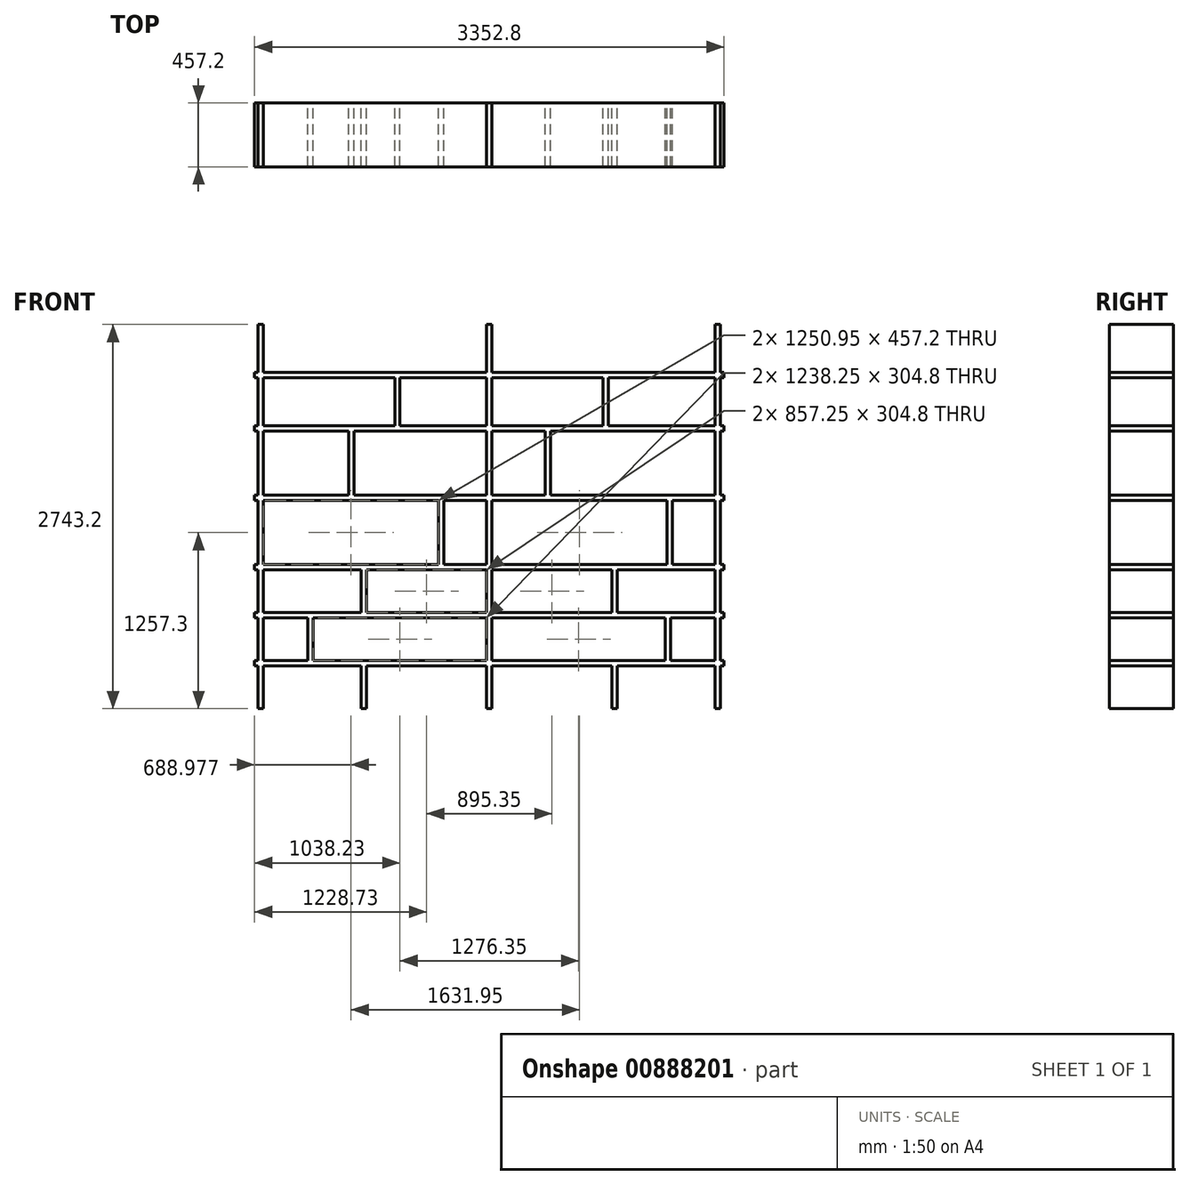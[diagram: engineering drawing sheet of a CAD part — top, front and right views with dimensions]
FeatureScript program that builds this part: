
annotation { "Feature Type Name" : "Feature", "Feature Type Description" : "" }
export const myFeature = defineFeature(function(context is Context, id is Id, definition is map)
    precondition{}
    {
        {
            var Q0;
            Q0=qCreatedBy(makeId("Front.planeOp"),FACE);
            var sketch = newSketch(context, id + "F0", { "sketchPlane" : qUnion([Q0])});
            skLineSegment(sketch, "E0.bottom", {"start": v(-54.9, 2702.76) * mm, "end": v(3297.9, 2702.76) * mm});
            skLineSegment(sketch, "E0.top", {"start": v(-54.9, -40.44) * mm, "end": v(3297.9, -40.44) * mm});
            skLineSegment(sketch, "E0.left", {"start": v(-54.9, 2702.76) * mm, "end": v(-54.9, -40.44) * mm});
            skLineSegment(sketch, "E0.right", {"start": v(3297.9, 2702.76) * mm, "end": v(3297.9, -40.44) * mm});
            skLineSegment(sketch, "E1", {"start": v(-54.9, 264.36) * mm, "end": v(3297.9, 264.36) * mm});
            skLineSegment(sketch, "E2", {"start": v(-54.9, 607.26) * mm, "end": v(3297.9, 607.26) * mm});
            skLineSegment(sketch, "E3", {"start": v(-54.9, 950.16) * mm, "end": v(3297.9, 950.16) * mm});
            skLineSegment(sketch, "E4", {"start": v(-54.9, 645.36) * mm, "end": v(3297.9, 645.36) * mm});
            skLineSegment(sketch, "E5", {"start": v(-54.9, 302.46) * mm, "end": v(3297.9, 302.46) * mm});
            skLineSegment(sketch, "E6", {"start": v(-54.9, 988.26) * mm, "end": v(3297.9, 988.26) * mm});
            skLineSegment(sketch, "E7", {"start": v(-54.9, 1445.46) * mm, "end": v(3297.9, 1445.46) * mm});
            skLineSegment(sketch, "E8", {"start": v(-54.9, 1483.56) * mm, "end": v(3297.9, 1483.56) * mm});
            skLineSegment(sketch, "E9", {"start": v(-54.9, 1940.76) * mm, "end": v(3297.9, 1940.76) * mm});
            skLineSegment(sketch, "E10", {"start": v(-54.9, 1978.86) * mm, "end": v(3297.9, 1978.86) * mm});
            skLineSegment(sketch, "E11", {"start": v(-54.9, 2321.76) * mm, "end": v(3297.9, 2321.76) * mm});
            skLineSegment(sketch, "E12", {"start": v(-54.9, 2359.86) * mm, "end": v(3297.9, 2359.86) * mm});
            skLineSegment(sketch, "E13.bottom", {"start": v(707.1, -40.44) * mm, "end": v(745.2, -40.44) * mm});
            skLineSegment(sketch, "E13.top", {"start": v(707.1, 264.36) * mm, "end": v(745.2, 264.36) * mm});
            skLineSegment(sketch, "E13.left", {"start": v(707.1, -40.44) * mm, "end": v(707.1, 264.36) * mm});
            skLineSegment(sketch, "E13.right", {"start": v(745.2, -40.44) * mm, "end": v(745.2, 264.36) * mm});
            skLineSegment(sketch, "E14.bottom", {"start": v(1602.45, -40.44) * mm, "end": v(1640.55, -40.44) * mm});
            skLineSegment(sketch, "E14.top", {"start": v(1602.45, 264.36) * mm, "end": v(1640.55, 264.36) * mm});
            skLineSegment(sketch, "E14.left", {"start": v(1602.45, -40.44) * mm, "end": v(1602.45, 264.36) * mm});
            skLineSegment(sketch, "E14.right", {"start": v(1640.55, -40.44) * mm, "end": v(1640.55, 264.36) * mm});
            skLineSegment(sketch, "E15.bottom", {"start": v(2497.8, -40.44) * mm, "end": v(2535.9, -40.44) * mm});
            skLineSegment(sketch, "E15.top", {"start": v(2497.8, 264.36) * mm, "end": v(2535.9, 264.36) * mm});
            skLineSegment(sketch, "E15.left", {"start": v(2497.8, -40.44) * mm, "end": v(2497.8, 264.36) * mm});
            skLineSegment(sketch, "E15.right", {"start": v(2535.9, -40.44) * mm, "end": v(2535.9, 264.36) * mm});
            skLineSegment(sketch, "E16.bottom", {"start": v(326.1, 302.46) * mm, "end": v(364.2, 302.46) * mm});
            skLineSegment(sketch, "E16.top", {"start": v(326.1, 607.26) * mm, "end": v(364.2, 607.26) * mm});
            skLineSegment(sketch, "E16.left", {"start": v(326.1, 302.46) * mm, "end": v(326.1, 607.26) * mm});
            skLineSegment(sketch, "E16.right", {"start": v(364.2, 302.46) * mm, "end": v(364.2, 607.26) * mm});
            skLineSegment(sketch, "E17.bottom", {"start": v(1640.55, 607.26) * mm, "end": v(1602.45, 607.26) * mm});
            skLineSegment(sketch, "E17.top", {"start": v(1640.55, 302.46) * mm, "end": v(1602.45, 302.46) * mm});
            skLineSegment(sketch, "E17.left", {"start": v(1640.55, 607.26) * mm, "end": v(1640.55, 302.46) * mm});
            skLineSegment(sketch, "E17.right", {"start": v(1602.45, 607.26) * mm, "end": v(1602.45, 302.46) * mm});
            skLineSegment(sketch, "E18.bottom", {"start": v(2878.8, 607.26) * mm, "end": v(2916.9, 607.26) * mm});
            skLineSegment(sketch, "E18.top", {"start": v(2878.8, 302.46) * mm, "end": v(2916.9, 302.46) * mm});
            skLineSegment(sketch, "E18.left", {"start": v(2878.8, 607.26) * mm, "end": v(2878.8, 302.46) * mm});
            skLineSegment(sketch, "E18.right", {"start": v(2916.9, 607.26) * mm, "end": v(2916.9, 302.46) * mm});
            skLineSegment(sketch, "E19.bottom", {"start": v(1259.55, 988.26) * mm, "end": v(1297.65, 988.26) * mm});
            skLineSegment(sketch, "E19.top", {"start": v(1259.55, 1445.46) * mm, "end": v(1297.65, 1445.46) * mm});
            skLineSegment(sketch, "E19.left", {"start": v(1297.65, 988.26) * mm, "end": v(1297.65, 1445.46) * mm});
            skLineSegment(sketch, "E19.right", {"start": v(1259.55, 1445.46) * mm, "end": v(1259.55, 988.26) * mm});
            skLineSegment(sketch, "E20.bottom", {"start": v(745.2, 950.16) * mm, "end": v(707.1, 950.16) * mm});
            skLineSegment(sketch, "E20.top", {"start": v(745.2, 645.36) * mm, "end": v(707.1, 645.36) * mm});
            skLineSegment(sketch, "E20.left", {"start": v(745.2, 950.16) * mm, "end": v(745.2, 645.36) * mm});
            skLineSegment(sketch, "E20.right", {"start": v(707.1, 950.16) * mm, "end": v(707.1, 645.36) * mm});
            skLineSegment(sketch, "E21.bottom", {"start": v(2497.8, 950.16) * mm, "end": v(2535.9, 950.16) * mm});
            skLineSegment(sketch, "E21.top", {"start": v(2497.8, 645.36) * mm, "end": v(2535.9, 645.36) * mm});
            skLineSegment(sketch, "E21.left", {"start": v(2497.8, 950.16) * mm, "end": v(2497.8, 645.36) * mm});
            skLineSegment(sketch, "E21.right", {"start": v(2535.9, 950.16) * mm, "end": v(2535.9, 645.36) * mm});
            skLineSegment(sketch, "E22.bottom", {"start": v(1602.45, 645.36) * mm, "end": v(1640.55, 645.36) * mm});
            skLineSegment(sketch, "E22.top", {"start": v(1602.45, 950.16) * mm, "end": v(1640.55, 950.16) * mm});
            skLineSegment(sketch, "E22.left", {"start": v(1602.45, 645.36) * mm, "end": v(1602.45, 950.16) * mm});
            skLineSegment(sketch, "E22.right", {"start": v(1640.55, 645.36) * mm, "end": v(1640.55, 950.16) * mm});
            skLineSegment(sketch, "E23.bottom", {"start": v(3272.5, 2702.76) * mm, "end": v(3234.4, 2702.76) * mm});
            skLineSegment(sketch, "E23.top", {"start": v(3272.5, -40.44) * mm, "end": v(3234.4, -40.44) * mm});
            skLineSegment(sketch, "E23.left", {"start": v(3272.5, 2702.76) * mm, "end": v(3272.5, -40.44) * mm});
            skLineSegment(sketch, "E23.right", {"start": v(3234.4, 2702.76) * mm, "end": v(3234.4, -40.44) * mm});
            skLineSegment(sketch, "E24.bottom", {"start": v(8.6, 2702.76) * mm, "end": v(-29.5, 2702.76) * mm});
            skLineSegment(sketch, "E24.top", {"start": v(8.6, -40.44) * mm, "end": v(-29.5, -40.44) * mm});
            skLineSegment(sketch, "E24.left", {"start": v(8.6, 2702.76) * mm, "end": v(8.6, -40.44) * mm});
            skLineSegment(sketch, "E24.right", {"start": v(-29.5, 2702.76) * mm, "end": v(-29.5, -40.44) * mm});
            skLineSegment(sketch, "E25.bottom", {"start": v(1640.55, 950.16) * mm, "end": v(1602.45, 950.16) * mm});
            skLineSegment(sketch, "E25.top", {"start": v(1640.55, 2702.76) * mm, "end": v(1602.45, 2702.76) * mm});
            skLineSegment(sketch, "E25.left", {"start": v(1640.55, 950.16) * mm, "end": v(1640.55, 2702.76) * mm});
            skLineSegment(sketch, "E25.right", {"start": v(1602.45, 950.16) * mm, "end": v(1602.45, 2702.76) * mm});
            skLineSegment(sketch, "E26.bottom", {"start": v(2891.5, 1445.46) * mm, "end": v(2929.6, 1445.46) * mm});
            skLineSegment(sketch, "E26.top", {"start": v(2891.5, 988.26) * mm, "end": v(2929.6, 988.26) * mm});
            skLineSegment(sketch, "E26.left", {"start": v(2891.5, 1445.46) * mm, "end": v(2891.5, 988.26) * mm});
            skLineSegment(sketch, "E26.right", {"start": v(2929.6, 1445.46) * mm, "end": v(2929.6, 988.26) * mm});
            skLineSegment(sketch, "E27.bottom", {"start": v(2021.55, 1483.56) * mm, "end": v(2059.65, 1483.56) * mm});
            skLineSegment(sketch, "E27.top", {"start": v(2021.55, 1940.76) * mm, "end": v(2059.65, 1940.76) * mm});
            skLineSegment(sketch, "E27.left", {"start": v(2021.55, 1483.56) * mm, "end": v(2021.55, 1940.76) * mm});
            skLineSegment(sketch, "E27.right", {"start": v(2059.65, 1483.56) * mm, "end": v(2059.65, 1940.76) * mm});
            skLineSegment(sketch, "E28.bottom", {"start": v(656.3, 1483.56) * mm, "end": v(618.2, 1483.56) * mm});
            skLineSegment(sketch, "E28.top", {"start": v(656.3, 1940.76) * mm, "end": v(618.2, 1940.76) * mm});
            skLineSegment(sketch, "E28.left", {"start": v(656.3, 1483.56) * mm, "end": v(656.3, 1940.76) * mm});
            skLineSegment(sketch, "E28.right", {"start": v(618.2, 1483.56) * mm, "end": v(618.2, 1940.76) * mm});
            skLineSegment(sketch, "E29.bottom", {"start": v(2472.4, 1978.86) * mm, "end": v(2434.3, 1978.86) * mm});
            skLineSegment(sketch, "E29.top", {"start": v(2472.4, 2321.76) * mm, "end": v(2434.3, 2321.76) * mm});
            skLineSegment(sketch, "E29.left", {"start": v(2472.4, 1978.86) * mm, "end": v(2472.4, 2321.76) * mm});
            skLineSegment(sketch, "E29.right", {"start": v(2434.3, 1978.86) * mm, "end": v(2434.3, 2321.76) * mm});
            skLineSegment(sketch, "E30.bottom", {"start": v(983.52, 2321.76) * mm, "end": v(945.42, 2321.76) * mm});
            skLineSegment(sketch, "E30.top", {"start": v(983.52, 1978.86) * mm, "end": v(945.42, 1978.86) * mm});
            skLineSegment(sketch, "E30.left", {"start": v(983.52, 2321.76) * mm, "end": v(983.52, 1978.86) * mm});
            skLineSegment(sketch, "E30.right", {"start": v(945.42, 2321.76) * mm, "end": v(945.42, 1978.86) * mm});
            skSolve(sketch);
        }
        {
            var Q0;
            {var subQ0=sQuery(id+"F0.wireOp",EDGE,"E24.left");var subQ1=sQuery(id+"F0.wireOp",EDGE,"E0.bottom");var subQ2=makeQuery(id+"F0.imprint","INTERSECT",VERTEX,{"derivedFrom":[subQ1,subQ0]});Q0=makeQuery(id+"F0.imprint","IMPRINT",FACE,{"disambiguationData":[TD([[makeQuery(id+"F0.imprint","IMPRINT",EDGE,{"disambiguationData":[TD([[subQ2,1.0]])],"derivedFrom":subQ1}),-1.0]])]});}
            var Q1;
            {var subQ0=sQuery(id+"F0.wireOp",EDGE,"E11");var subQ1=sQuery(id+"F0.wireOp",EDGE,"E0.left");var subQ2=makeQuery(id+"F0.imprint","INTERSECT",VERTEX,{"derivedFrom":[subQ1,subQ0]});Q1=makeQuery(id+"F0.imprint","IMPRINT",FACE,{"disambiguationData":[TD([[makeQuery(id+"F0.imprint","IMPRINT",EDGE,{"disambiguationData":[TD([[subQ2,1.0]])],"derivedFrom":subQ1}),1.0]])]});}
            var Q2;
            {var subQ0=sQuery(id+"F0.wireOp",EDGE,"E24.left");var subQ1=sQuery(id+"F0.wireOp",EDGE,"E11");var subQ2=makeQuery(id+"F0.imprint","INTERSECT",VERTEX,{"derivedFrom":[subQ1,subQ0]});Q2=makeQuery(id+"F0.imprint","IMPRINT",FACE,{"disambiguationData":[TD([[makeQuery(id+"F0.imprint","IMPRINT",EDGE,{"disambiguationData":[TD([[subQ2,1.0]])],"derivedFrom":subQ1}),1.0]])]});}
            var Q3;
            {var subQ3=sQuery(id+"F0.wireOp",EDGE,"E24.left");var subQ5=sQuery(id+"F0.wireOp",EDGE,"E11");var subQ8=makeQuery(id+"F0.imprint","INTERSECT",VERTEX,{"derivedFrom":[subQ5,subQ3]});Q3=makeQuery(id+"F0.imprint","IMPRINT",FACE,{"disambiguationData":[TD([[makeQuery(id+"F0.imprint","IMPRINT",EDGE,{"disambiguationData":[TD([[subQ8,-1.0]])],"derivedFrom":subQ5}),1.0]])]});}
            var Q4;
            {var subQ0=sQuery(id+"F0.wireOp",EDGE,"E24.left");var subQ1=sQuery(id+"F0.wireOp",EDGE,"E10");var subQ2=makeQuery(id+"F0.imprint","INTERSECT",VERTEX,{"derivedFrom":[subQ1,subQ0]});Q4=makeQuery(id+"F0.imprint","IMPRINT",FACE,{"disambiguationData":[TD([[makeQuery(id+"F0.imprint","IMPRINT",EDGE,{"disambiguationData":[TD([[subQ2,1.0]])],"derivedFrom":subQ1}),1.0]])]});}
            var Q5;
            {var subQ0=sQuery(id+"F0.wireOp",EDGE,"E25.left");var subQ1=sQuery(id+"F0.wireOp",EDGE,"E0.bottom");var subQ2=makeQuery(id+"F0.imprint","INTERSECT",VERTEX,{"derivedFrom":[subQ1,subQ0]});Q5=makeQuery(id+"F0.imprint","IMPRINT",FACE,{"disambiguationData":[TD([[makeQuery(id+"F0.imprint","IMPRINT",EDGE,{"disambiguationData":[TD([[subQ2,1.0]])],"derivedFrom":subQ1}),-1.0]])]});}
            var Q6;
            {var subQ0=sQuery(id+"F0.wireOp",EDGE,"E25.left");var subQ1=sQuery(id+"F0.wireOp",EDGE,"E11");var subQ2=makeQuery(id+"F0.imprint","INTERSECT",VERTEX,{"derivedFrom":[subQ1,subQ0]});Q6=makeQuery(id+"F0.imprint","IMPRINT",FACE,{"disambiguationData":[TD([[makeQuery(id+"F0.imprint","IMPRINT",EDGE,{"disambiguationData":[TD([[subQ2,1.0]])],"derivedFrom":subQ1}),1.0]])]});}
            var Q7;
            {var subQ0=sQuery(id+"F0.wireOp",EDGE,"E11");var subQ8=makeQuery(id+"F0.imprint","INTERSECT",VERTEX,{"derivedFrom":[subQ0,sQuery(id+"F0.wireOp",EDGE,"E29.right")]});Q7=makeQuery(id+"F0.imprint","IMPRINT",FACE,{"disambiguationData":[TD([[makeQuery(id+"F0.imprint","IMPRINT",EDGE,{"disambiguationData":[TD([[subQ8,1.0]])],"derivedFrom":subQ0}),1.0]])]});}
            var Q8;
            {var subQ0=sQuery(id+"F0.wireOp",EDGE,"E25.left");var subQ1=sQuery(id+"F0.wireOp",EDGE,"E10");var subQ2=makeQuery(id+"F0.imprint","INTERSECT",VERTEX,{"derivedFrom":[subQ1,subQ0]});Q8=makeQuery(id+"F0.imprint","IMPRINT",FACE,{"disambiguationData":[TD([[makeQuery(id+"F0.imprint","IMPRINT",EDGE,{"disambiguationData":[TD([[subQ2,1.0]])],"derivedFrom":subQ1}),1.0]])]});}
            var Q9;
            {var subQ0=sQuery(id+"F0.wireOp",EDGE,"E30.left");Q9=makeQuery(id+"F0.imprint","IMPRINT",FACE,{"disambiguationData":[TD([[makeQuery(id+"F0.imprint","IMPRINT",EDGE,{"derivedFrom":subQ0}),-1.0]])]});}
            var Q10;
            {var subQ0=sQuery(id+"F0.wireOp",EDGE,"E9");var subQ1=makeQuery(id+"F0.imprint","INTERSECT",VERTEX,{"derivedFrom":[subQ0,sQuery(id+"F0.wireOp",EDGE,"E28.left")]});Q10=makeQuery(id+"F0.imprint","IMPRINT",FACE,{"disambiguationData":[TD([[makeQuery(id+"F0.imprint","IMPRINT",EDGE,{"disambiguationData":[TD([[subQ1,-1.0]])],"derivedFrom":subQ0}),1.0]])]});}
            var Q11;
            {var subQ0=sQuery(id+"F0.wireOp",EDGE,"E24.left");var subQ1=sQuery(id+"F0.wireOp",EDGE,"E9");var subQ2=makeQuery(id+"F0.imprint","INTERSECT",VERTEX,{"derivedFrom":[subQ1,subQ0]});Q11=makeQuery(id+"F0.imprint","IMPRINT",FACE,{"disambiguationData":[TD([[makeQuery(id+"F0.imprint","IMPRINT",EDGE,{"disambiguationData":[TD([[subQ2,1.0]])],"derivedFrom":subQ1}),1.0]])]});}
            var Q12;
            {var subQ0=sQuery(id+"F0.wireOp",EDGE,"E9");var subQ1=sQuery(id+"F0.wireOp",EDGE,"E0.left");var subQ2=makeQuery(id+"F0.imprint","INTERSECT",VERTEX,{"derivedFrom":[subQ1,subQ0]});Q12=makeQuery(id+"F0.imprint","IMPRINT",FACE,{"disambiguationData":[TD([[makeQuery(id+"F0.imprint","IMPRINT",EDGE,{"disambiguationData":[TD([[subQ2,1.0]])],"derivedFrom":subQ1}),1.0]])]});}
            var Q13;
            {var subQ0=sQuery(id+"F0.wireOp",EDGE,"E24.left");var subQ1=sQuery(id+"F0.wireOp",EDGE,"E8");var subQ2=makeQuery(id+"F0.imprint","INTERSECT",VERTEX,{"derivedFrom":[subQ1,subQ0]});Q13=makeQuery(id+"F0.imprint","IMPRINT",FACE,{"disambiguationData":[TD([[makeQuery(id+"F0.imprint","IMPRINT",EDGE,{"disambiguationData":[TD([[subQ2,1.0]])],"derivedFrom":subQ1}),1.0]])]});}
            var Q14;
            {var subQ0=sQuery(id+"F0.wireOp",EDGE,"E28.left");Q14=makeQuery(id+"F0.imprint","IMPRINT",FACE,{"disambiguationData":[TD([[makeQuery(id+"F0.imprint","IMPRINT",EDGE,{"derivedFrom":subQ0}),1.0]])]});}
            var Q15;
            {var subQ0=sQuery(id+"F0.wireOp",EDGE,"E24.left");var subQ1=sQuery(id+"F0.wireOp",EDGE,"E7");var subQ2=makeQuery(id+"F0.imprint","INTERSECT",VERTEX,{"derivedFrom":[subQ1,subQ0]});Q15=makeQuery(id+"F0.imprint","IMPRINT",FACE,{"disambiguationData":[TD([[makeQuery(id+"F0.imprint","IMPRINT",EDGE,{"disambiguationData":[TD([[subQ2,1.0]])],"derivedFrom":subQ1}),1.0]])]});}
            var Q16;
            {var subQ4=sQuery(id+"F0.wireOp",EDGE,"E7");var subQ5=makeQuery(id+"F0.imprint","INTERSECT",VERTEX,{"derivedFrom":[subQ4,sQuery(id+"F0.wireOp",EDGE,"E19.right")]});Q16=makeQuery(id+"F0.imprint","IMPRINT",FACE,{"disambiguationData":[TD([[makeQuery(id+"F0.imprint","IMPRINT",EDGE,{"disambiguationData":[TD([[subQ5,1.0]])],"derivedFrom":subQ4}),1.0]])]});}
            var Q17;
            {var subQ0=sQuery(id+"F0.wireOp",EDGE,"E24.left");var subQ1=sQuery(id+"F0.wireOp",EDGE,"E6");var subQ2=makeQuery(id+"F0.imprint","INTERSECT",VERTEX,{"derivedFrom":[subQ1,subQ0]});Q17=makeQuery(id+"F0.imprint","IMPRINT",FACE,{"disambiguationData":[TD([[makeQuery(id+"F0.imprint","IMPRINT",EDGE,{"disambiguationData":[TD([[subQ2,1.0]])],"derivedFrom":subQ1}),1.0]])]});}
            var Q18;
            {var subQ0=sQuery(id+"F0.wireOp",EDGE,"E7");var subQ1=sQuery(id+"F0.wireOp",EDGE,"E0.left");var subQ2=makeQuery(id+"F0.imprint","INTERSECT",VERTEX,{"derivedFrom":[subQ1,subQ0]});Q18=makeQuery(id+"F0.imprint","IMPRINT",FACE,{"disambiguationData":[TD([[makeQuery(id+"F0.imprint","IMPRINT",EDGE,{"disambiguationData":[TD([[subQ2,1.0]])],"derivedFrom":subQ1}),1.0]])]});}
            var Q19;
            {var subQ0=sQuery(id+"F0.wireOp",EDGE,"E3");var subQ1=sQuery(id+"F0.wireOp",EDGE,"E0.left");var subQ2=makeQuery(id+"F0.imprint","INTERSECT",VERTEX,{"derivedFrom":[subQ1,subQ0]});Q19=makeQuery(id+"F0.imprint","IMPRINT",FACE,{"disambiguationData":[TD([[makeQuery(id+"F0.imprint","IMPRINT",EDGE,{"disambiguationData":[TD([[subQ2,1.0]])],"derivedFrom":subQ1}),1.0]])]});}
            var Q20;
            {var subQ0=sQuery(id+"F0.wireOp",EDGE,"E2");var subQ1=sQuery(id+"F0.wireOp",EDGE,"E0.left");var subQ2=makeQuery(id+"F0.imprint","INTERSECT",VERTEX,{"derivedFrom":[subQ1,subQ0]});Q20=makeQuery(id+"F0.imprint","IMPRINT",FACE,{"disambiguationData":[TD([[makeQuery(id+"F0.imprint","IMPRINT",EDGE,{"disambiguationData":[TD([[subQ2,1.0]])],"derivedFrom":subQ1}),1.0]])]});}
            var Q21;
            {var subQ0=sQuery(id+"F0.wireOp",EDGE,"E24.left");var subQ1=sQuery(id+"F0.wireOp",EDGE,"E0.top");var subQ2=makeQuery(id+"F0.imprint","INTERSECT",VERTEX,{"derivedFrom":[subQ1,subQ0]});Q21=makeQuery(id+"F0.imprint","IMPRINT",FACE,{"disambiguationData":[TD([[makeQuery(id+"F0.imprint","IMPRINT",EDGE,{"disambiguationData":[TD([[subQ2,1.0]])],"derivedFrom":subQ1}),1.0]])]});}
            var Q22;
            {var subQ0=sQuery(id+"F0.wireOp",EDGE,"E5");var subQ1=sQuery(id+"F0.wireOp",EDGE,"E0.left");var subQ2=makeQuery(id+"F0.imprint","INTERSECT",VERTEX,{"derivedFrom":[subQ1,subQ0]});Q22=makeQuery(id+"F0.imprint","IMPRINT",FACE,{"disambiguationData":[TD([[makeQuery(id+"F0.imprint","IMPRINT",EDGE,{"disambiguationData":[TD([[subQ2,-1.0]])],"derivedFrom":subQ1}),1.0]])]});}
            var Q23;
            {var subQ0=sQuery(id+"F0.wireOp",EDGE,"E24.left");var subQ1=sQuery(id+"F0.wireOp",EDGE,"E1");var subQ2=makeQuery(id+"F0.imprint","INTERSECT",VERTEX,{"derivedFrom":[subQ1,subQ0]});Q23=makeQuery(id+"F0.imprint","IMPRINT",FACE,{"disambiguationData":[TD([[makeQuery(id+"F0.imprint","IMPRINT",EDGE,{"disambiguationData":[TD([[subQ2,1.0]])],"derivedFrom":subQ1}),1.0]])]});}
            var Q24;
            {var subQ0=sQuery(id+"F0.wireOp",EDGE,"E24.left");var subQ1=sQuery(id+"F0.wireOp",EDGE,"E2");var subQ2=makeQuery(id+"F0.imprint","INTERSECT",VERTEX,{"derivedFrom":[subQ1,subQ0]});Q24=makeQuery(id+"F0.imprint","IMPRINT",FACE,{"disambiguationData":[TD([[makeQuery(id+"F0.imprint","IMPRINT",EDGE,{"disambiguationData":[TD([[subQ2,1.0]])],"derivedFrom":subQ1}),-1.0]])]});}
            var Q25;
            {var subQ0=sQuery(id+"F0.wireOp",EDGE,"E24.left");var subQ1=sQuery(id+"F0.wireOp",EDGE,"E2");var subQ2=makeQuery(id+"F0.imprint","INTERSECT",VERTEX,{"derivedFrom":[subQ1,subQ0]});Q25=makeQuery(id+"F0.imprint","IMPRINT",FACE,{"disambiguationData":[TD([[makeQuery(id+"F0.imprint","IMPRINT",EDGE,{"disambiguationData":[TD([[subQ2,1.0]])],"derivedFrom":subQ1}),1.0]])]});}
            var Q26;
            {var subQ0=sQuery(id+"F0.wireOp",EDGE,"E24.left");var subQ1=sQuery(id+"F0.wireOp",EDGE,"E3");var subQ2=makeQuery(id+"F0.imprint","INTERSECT",VERTEX,{"derivedFrom":[subQ1,subQ0]});Q26=makeQuery(id+"F0.imprint","IMPRINT",FACE,{"disambiguationData":[TD([[makeQuery(id+"F0.imprint","IMPRINT",EDGE,{"disambiguationData":[TD([[subQ2,1.0]])],"derivedFrom":subQ1}),-1.0]])]});}
            var Q27;
            {var subQ0=sQuery(id+"F0.wireOp",EDGE,"E2");var subQ1=makeQuery(id+"F0.imprint","INTERSECT",VERTEX,{"derivedFrom":[subQ0,sQuery(id+"F0.wireOp",EDGE,"E16.right")]});Q27=makeQuery(id+"F0.imprint","IMPRINT",FACE,{"disambiguationData":[TD([[makeQuery(id+"F0.imprint","IMPRINT",EDGE,{"disambiguationData":[TD([[subQ1,-1.0]])],"derivedFrom":subQ0}),1.0]])]});}
            var Q28;
            {var subQ4=sQuery(id+"F0.wireOp",EDGE,"E3");var subQ8=makeQuery(id+"F0.imprint","INTERSECT",VERTEX,{"derivedFrom":[subQ4,sQuery(id+"F0.wireOp",EDGE,"E20.right")]});Q28=makeQuery(id+"F0.imprint","IMPRINT",FACE,{"disambiguationData":[TD([[makeQuery(id+"F0.imprint","IMPRINT",EDGE,{"disambiguationData":[TD([[subQ8,1.0]])],"derivedFrom":subQ4}),1.0]])]});}
            var Q29;
            {var subQ0=sQuery(id+"F0.wireOp",EDGE,"E20.left");Q29=makeQuery(id+"F0.imprint","IMPRINT",FACE,{"disambiguationData":[TD([[makeQuery(id+"F0.imprint","IMPRINT",EDGE,{"derivedFrom":subQ0}),-1.0]])]});}
            var Q30;
            {var subQ0=sQuery(id+"F0.wireOp",EDGE,"E24.left");var subQ1=sQuery(id+"F0.wireOp",EDGE,"E3");var subQ2=makeQuery(id+"F0.imprint","INTERSECT",VERTEX,{"derivedFrom":[subQ1,subQ0]});Q30=makeQuery(id+"F0.imprint","IMPRINT",FACE,{"disambiguationData":[TD([[makeQuery(id+"F0.imprint","IMPRINT",EDGE,{"disambiguationData":[TD([[subQ2,1.0]])],"derivedFrom":subQ1}),1.0]])]});}
            var Q31;
            {var subQ2=sQuery(id+"F0.wireOp",EDGE,"E16.left");Q31=makeQuery(id+"F0.imprint","IMPRINT",FACE,{"disambiguationData":[TD([[makeQuery(id+"F0.imprint","IMPRINT",EDGE,{"derivedFrom":subQ2}),-1.0]])]});}
            var Q32;
            {var subQ0=sQuery(id+"F0.wireOp",EDGE,"E1");var subQ7=makeQuery(id+"F0.imprint","INTERSECT",VERTEX,{"derivedFrom":[subQ0,sQuery(id+"F0.wireOp",EDGE,"E14.right")]});Q32=makeQuery(id+"F0.imprint","IMPRINT",FACE,{"disambiguationData":[TD([[makeQuery(id+"F0.imprint","IMPRINT",EDGE,{"disambiguationData":[TD([[subQ7,-1.0]])],"derivedFrom":subQ0}),1.0]])]});}
            var Q33;
            {var subQ0=sQuery(id+"F0.wireOp",EDGE,"E13.left");Q33=makeQuery(id+"F0.imprint","IMPRINT",FACE,{"disambiguationData":[TD([[makeQuery(id+"F0.imprint","IMPRINT",EDGE,{"derivedFrom":subQ0}),-1.0]])]});}
            var Q34;
            {var subQ0=sQuery(id+"F0.wireOp",EDGE,"E19.left");Q34=makeQuery(id+"F0.imprint","IMPRINT",FACE,{"disambiguationData":[TD([[makeQuery(id+"F0.imprint","IMPRINT",EDGE,{"derivedFrom":subQ0}),1.0]])]});}
            var Q35;
            {var subQ0=sQuery(id+"F0.wireOp",EDGE,"E25.right");var subQ1=sQuery(id+"F0.wireOp",EDGE,"E9");var subQ2=makeQuery(id+"F0.imprint","INTERSECT",VERTEX,{"derivedFrom":[subQ1,subQ0]});Q35=makeQuery(id+"F0.imprint","IMPRINT",FACE,{"disambiguationData":[TD([[makeQuery(id+"F0.imprint","IMPRINT",EDGE,{"disambiguationData":[TD([[subQ2,-1.0]])],"derivedFrom":subQ1}),1.0]])]});}
            var Q36;
            {var subQ0=sQuery(id+"F0.wireOp",EDGE,"E25.right");var subQ1=sQuery(id+"F0.wireOp",EDGE,"E8");var subQ2=makeQuery(id+"F0.imprint","INTERSECT",VERTEX,{"derivedFrom":[subQ1,subQ0]});Q36=makeQuery(id+"F0.imprint","IMPRINT",FACE,{"disambiguationData":[TD([[makeQuery(id+"F0.imprint","IMPRINT",EDGE,{"disambiguationData":[TD([[subQ2,-1.0]])],"derivedFrom":subQ1}),1.0]])]});}
            var Q37;
            {var subQ0=sQuery(id+"F0.wireOp",EDGE,"E25.left");var subQ1=sQuery(id+"F0.wireOp",EDGE,"E7");var subQ2=makeQuery(id+"F0.imprint","INTERSECT",VERTEX,{"derivedFrom":[subQ1,subQ0]});Q37=makeQuery(id+"F0.imprint","IMPRINT",FACE,{"disambiguationData":[TD([[makeQuery(id+"F0.imprint","IMPRINT",EDGE,{"disambiguationData":[TD([[subQ2,1.0]])],"derivedFrom":subQ1}),1.0]])]});}
            var Q38;
            {var subQ0=sQuery(id+"F0.wireOp",EDGE,"E25.left");var subQ1=sQuery(id+"F0.wireOp",EDGE,"E6");var subQ2=makeQuery(id+"F0.imprint","INTERSECT",VERTEX,{"derivedFrom":[subQ1,subQ0]});Q38=makeQuery(id+"F0.imprint","IMPRINT",FACE,{"disambiguationData":[TD([[makeQuery(id+"F0.imprint","IMPRINT",EDGE,{"disambiguationData":[TD([[subQ2,1.0]])],"derivedFrom":subQ1}),1.0]])]});}
            var Q39;
            {var subQ0=sQuery(id+"F0.wireOp",EDGE,"E25.left");var subQ5=sQuery(id+"F0.wireOp",EDGE,"E6");var subQ6=makeQuery(id+"F0.imprint","INTERSECT",VERTEX,{"derivedFrom":[subQ5,subQ0]});Q39=makeQuery(id+"F0.imprint","IMPRINT",FACE,{"disambiguationData":[TD([[makeQuery(id+"F0.imprint","IMPRINT",EDGE,{"disambiguationData":[TD([[subQ6,1.0]])],"derivedFrom":subQ5}),-1.0]])]});}
            var Q40;
            {var subQ2=sQuery(id+"F0.wireOp",EDGE,"E22.left");Q40=makeQuery(id+"F0.imprint","IMPRINT",FACE,{"disambiguationData":[TD([[makeQuery(id+"F0.imprint","IMPRINT",EDGE,{"derivedFrom":subQ2}),-1.0]])]});}
            var Q41;
            {var subQ0=sQuery(id+"F0.wireOp",EDGE,"E17.left");Q41=makeQuery(id+"F0.imprint","IMPRINT",FACE,{"disambiguationData":[TD([[makeQuery(id+"F0.imprint","IMPRINT",EDGE,{"derivedFrom":subQ0}),-1.0]])]});}
            var Q42;
            {var subQ2=sQuery(id+"F0.wireOp",EDGE,"E14.left");Q42=makeQuery(id+"F0.imprint","IMPRINT",FACE,{"disambiguationData":[TD([[makeQuery(id+"F0.imprint","IMPRINT",EDGE,{"derivedFrom":subQ2}),-1.0]])]});}
            var Q43;
            {var subQ2=sQuery(id+"F0.wireOp",EDGE,"E27.left");Q43=makeQuery(id+"F0.imprint","IMPRINT",FACE,{"disambiguationData":[TD([[makeQuery(id+"F0.imprint","IMPRINT",EDGE,{"derivedFrom":subQ2}),-1.0]])]});}
            var Q44;
            {var subQ4=sQuery(id+"F0.wireOp",EDGE,"E9");var subQ5=makeQuery(id+"F0.imprint","INTERSECT",VERTEX,{"derivedFrom":[subQ4,sQuery(id+"F0.wireOp",EDGE,"E27.right")]});Q44=makeQuery(id+"F0.imprint","IMPRINT",FACE,{"disambiguationData":[TD([[makeQuery(id+"F0.imprint","IMPRINT",EDGE,{"disambiguationData":[TD([[subQ5,-1.0]])],"derivedFrom":subQ4}),1.0]])]});}
            var Q45;
            {var subQ0=sQuery(id+"F0.wireOp",EDGE,"E29.left");Q45=makeQuery(id+"F0.imprint","IMPRINT",FACE,{"disambiguationData":[TD([[makeQuery(id+"F0.imprint","IMPRINT",EDGE,{"derivedFrom":subQ0}),1.0]])]});}
            var Q46;
            {var subQ0=sQuery(id+"F0.wireOp",EDGE,"E23.right");var subQ1=sQuery(id+"F0.wireOp",EDGE,"E0.bottom");var subQ2=makeQuery(id+"F0.imprint","INTERSECT",VERTEX,{"derivedFrom":[subQ1,subQ0]});Q46=makeQuery(id+"F0.imprint","IMPRINT",FACE,{"disambiguationData":[TD([[makeQuery(id+"F0.imprint","IMPRINT",EDGE,{"disambiguationData":[TD([[subQ2,-1.0]])],"derivedFrom":subQ1}),-1.0]])]});}
            var Q47;
            {var subQ0=sQuery(id+"F0.wireOp",EDGE,"E23.right");var subQ1=sQuery(id+"F0.wireOp",EDGE,"E10");var subQ2=makeQuery(id+"F0.imprint","INTERSECT",VERTEX,{"derivedFrom":[subQ1,subQ0]});Q47=makeQuery(id+"F0.imprint","IMPRINT",FACE,{"disambiguationData":[TD([[makeQuery(id+"F0.imprint","IMPRINT",EDGE,{"disambiguationData":[TD([[subQ2,-1.0]])],"derivedFrom":subQ1}),1.0]])]});}
            var Q48;
            {var subQ0=sQuery(id+"F0.wireOp",EDGE,"E23.right");var subQ1=sQuery(id+"F0.wireOp",EDGE,"E8");var subQ2=makeQuery(id+"F0.imprint","INTERSECT",VERTEX,{"derivedFrom":[subQ1,subQ0]});Q48=makeQuery(id+"F0.imprint","IMPRINT",FACE,{"disambiguationData":[TD([[makeQuery(id+"F0.imprint","IMPRINT",EDGE,{"disambiguationData":[TD([[subQ2,-1.0]])],"derivedFrom":subQ1}),1.0]])]});}
            var Q49;
            {var subQ0=sQuery(id+"F0.wireOp",EDGE,"E26.left");Q49=makeQuery(id+"F0.imprint","IMPRINT",FACE,{"disambiguationData":[TD([[makeQuery(id+"F0.imprint","IMPRINT",EDGE,{"derivedFrom":subQ0}),1.0]])]});}
            var Q50;
            {var subQ4=sQuery(id+"F0.wireOp",EDGE,"E25.left");var subQ5=sQuery(id+"F0.wireOp",EDGE,"E7");var subQ6=makeQuery(id+"F0.imprint","INTERSECT",VERTEX,{"derivedFrom":[subQ5,subQ4]});Q50=makeQuery(id+"F0.imprint","IMPRINT",FACE,{"disambiguationData":[TD([[makeQuery(id+"F0.imprint","IMPRINT",EDGE,{"disambiguationData":[TD([[subQ6,-1.0]])],"derivedFrom":subQ5}),1.0]])]});}
            var Q51;
            {var subQ4=sQuery(id+"F0.wireOp",EDGE,"E3");var subQ7=makeQuery(id+"F0.imprint","INTERSECT",VERTEX,{"derivedFrom":[subQ4,sQuery(id+"F0.wireOp",EDGE,"E21.right")]});Q51=makeQuery(id+"F0.imprint","IMPRINT",FACE,{"disambiguationData":[TD([[makeQuery(id+"F0.imprint","IMPRINT",EDGE,{"disambiguationData":[TD([[subQ7,-1.0]])],"derivedFrom":subQ4}),1.0]])]});}
            var Q52;
            {var subQ0=sQuery(id+"F0.wireOp",EDGE,"E21.left");Q52=makeQuery(id+"F0.imprint","IMPRINT",FACE,{"disambiguationData":[TD([[makeQuery(id+"F0.imprint","IMPRINT",EDGE,{"derivedFrom":subQ0}),1.0]])]});}
            var Q53;
            {var subQ0=sQuery(id+"F0.wireOp",EDGE,"E18.left");Q53=makeQuery(id+"F0.imprint","IMPRINT",FACE,{"disambiguationData":[TD([[makeQuery(id+"F0.imprint","IMPRINT",EDGE,{"derivedFrom":subQ0}),1.0]])]});}
            var Q54;
            {var subQ0=sQuery(id+"F0.wireOp",EDGE,"E15.left");Q54=makeQuery(id+"F0.imprint","IMPRINT",FACE,{"disambiguationData":[TD([[makeQuery(id+"F0.imprint","IMPRINT",EDGE,{"derivedFrom":subQ0}),-1.0]])]});}
            var Q55;
            {var subQ0=sQuery(id+"F0.wireOp",EDGE,"E23.right");var subQ1=sQuery(id+"F0.wireOp",EDGE,"E0.top");var subQ2=makeQuery(id+"F0.imprint","INTERSECT",VERTEX,{"derivedFrom":[subQ1,subQ0]});Q55=makeQuery(id+"F0.imprint","IMPRINT",FACE,{"disambiguationData":[TD([[makeQuery(id+"F0.imprint","IMPRINT",EDGE,{"disambiguationData":[TD([[subQ2,-1.0]])],"derivedFrom":subQ1}),1.0]])]});}
            var Q56;
            {var subQ0=sQuery(id+"F0.wireOp",EDGE,"E23.right");var subQ1=sQuery(id+"F0.wireOp",EDGE,"E1");var subQ2=makeQuery(id+"F0.imprint","INTERSECT",VERTEX,{"derivedFrom":[subQ1,subQ0]});Q56=makeQuery(id+"F0.imprint","IMPRINT",FACE,{"disambiguationData":[TD([[makeQuery(id+"F0.imprint","IMPRINT",EDGE,{"disambiguationData":[TD([[subQ2,-1.0]])],"derivedFrom":subQ1}),1.0]])]});}
            var Q57;
            {var subQ0=sQuery(id+"F0.wireOp",EDGE,"E1");var subQ1=sQuery(id+"F0.wireOp",EDGE,"E0.right");var subQ2=makeQuery(id+"F0.imprint","INTERSECT",VERTEX,{"derivedFrom":[subQ1,subQ0]});Q57=makeQuery(id+"F0.imprint","IMPRINT",FACE,{"disambiguationData":[TD([[makeQuery(id+"F0.imprint","IMPRINT",EDGE,{"disambiguationData":[TD([[subQ2,1.0]])],"derivedFrom":subQ1}),-1.0]])]});}
            var Q58;
            {var subQ0=sQuery(id+"F0.wireOp",EDGE,"E23.left");var subQ1=sQuery(id+"F0.wireOp",EDGE,"E2");var subQ2=makeQuery(id+"F0.imprint","INTERSECT",VERTEX,{"derivedFrom":[subQ1,subQ0]});Q58=makeQuery(id+"F0.imprint","IMPRINT",FACE,{"disambiguationData":[TD([[makeQuery(id+"F0.imprint","IMPRINT",EDGE,{"disambiguationData":[TD([[subQ2,1.0]])],"derivedFrom":subQ1}),-1.0]])]});}
            var Q59;
            {var subQ0=sQuery(id+"F0.wireOp",EDGE,"E2");var subQ1=sQuery(id+"F0.wireOp",EDGE,"E0.right");var subQ2=makeQuery(id+"F0.imprint","INTERSECT",VERTEX,{"derivedFrom":[subQ1,subQ0]});Q59=makeQuery(id+"F0.imprint","IMPRINT",FACE,{"disambiguationData":[TD([[makeQuery(id+"F0.imprint","IMPRINT",EDGE,{"disambiguationData":[TD([[subQ2,1.0]])],"derivedFrom":subQ1}),-1.0]])]});}
            var Q60;
            {var subQ0=sQuery(id+"F0.wireOp",EDGE,"E23.left");var subQ1=sQuery(id+"F0.wireOp",EDGE,"E2");var subQ2=makeQuery(id+"F0.imprint","INTERSECT",VERTEX,{"derivedFrom":[subQ1,subQ0]});Q60=makeQuery(id+"F0.imprint","IMPRINT",FACE,{"disambiguationData":[TD([[makeQuery(id+"F0.imprint","IMPRINT",EDGE,{"disambiguationData":[TD([[subQ2,1.0]])],"derivedFrom":subQ1}),1.0]])]});}
            var Q61;
            {var subQ0=sQuery(id+"F0.wireOp",EDGE,"E23.right");var subQ1=sQuery(id+"F0.wireOp",EDGE,"E3");var subQ2=makeQuery(id+"F0.imprint","INTERSECT",VERTEX,{"derivedFrom":[subQ1,subQ0]});Q61=makeQuery(id+"F0.imprint","IMPRINT",FACE,{"disambiguationData":[TD([[makeQuery(id+"F0.imprint","IMPRINT",EDGE,{"disambiguationData":[TD([[subQ2,-1.0]])],"derivedFrom":subQ1}),-1.0]])]});}
            var Q62;
            {var subQ0=sQuery(id+"F0.wireOp",EDGE,"E23.right");var subQ1=sQuery(id+"F0.wireOp",EDGE,"E3");var subQ2=makeQuery(id+"F0.imprint","INTERSECT",VERTEX,{"derivedFrom":[subQ1,subQ0]});Q62=makeQuery(id+"F0.imprint","IMPRINT",FACE,{"disambiguationData":[TD([[makeQuery(id+"F0.imprint","IMPRINT",EDGE,{"disambiguationData":[TD([[subQ2,-1.0]])],"derivedFrom":subQ1}),1.0]])]});}
            var Q63;
            {var subQ0=sQuery(id+"F0.wireOp",EDGE,"E23.right");var subQ1=sQuery(id+"F0.wireOp",EDGE,"E6");var subQ2=makeQuery(id+"F0.imprint","INTERSECT",VERTEX,{"derivedFrom":[subQ1,subQ0]});Q63=makeQuery(id+"F0.imprint","IMPRINT",FACE,{"disambiguationData":[TD([[makeQuery(id+"F0.imprint","IMPRINT",EDGE,{"disambiguationData":[TD([[subQ2,-1.0]])],"derivedFrom":subQ1}),1.0]])]});}
            var Q64;
            {var subQ0=sQuery(id+"F0.wireOp",EDGE,"E23.left");var subQ1=sQuery(id+"F0.wireOp",EDGE,"E7");var subQ2=makeQuery(id+"F0.imprint","INTERSECT",VERTEX,{"derivedFrom":[subQ1,subQ0]});Q64=makeQuery(id+"F0.imprint","IMPRINT",FACE,{"disambiguationData":[TD([[makeQuery(id+"F0.imprint","IMPRINT",EDGE,{"disambiguationData":[TD([[subQ2,1.0]])],"derivedFrom":subQ1}),1.0]])]});}
            var Q65;
            {var subQ0=sQuery(id+"F0.wireOp",EDGE,"E3");var subQ1=sQuery(id+"F0.wireOp",EDGE,"E0.right");var subQ2=makeQuery(id+"F0.imprint","INTERSECT",VERTEX,{"derivedFrom":[subQ1,subQ0]});Q65=makeQuery(id+"F0.imprint","IMPRINT",FACE,{"disambiguationData":[TD([[makeQuery(id+"F0.imprint","IMPRINT",EDGE,{"disambiguationData":[TD([[subQ2,1.0]])],"derivedFrom":subQ1}),-1.0]])]});}
            var Q66;
            {var subQ0=sQuery(id+"F0.wireOp",EDGE,"E7");var subQ1=sQuery(id+"F0.wireOp",EDGE,"E0.right");var subQ2=makeQuery(id+"F0.imprint","INTERSECT",VERTEX,{"derivedFrom":[subQ1,subQ0]});Q66=makeQuery(id+"F0.imprint","IMPRINT",FACE,{"disambiguationData":[TD([[makeQuery(id+"F0.imprint","IMPRINT",EDGE,{"disambiguationData":[TD([[subQ2,1.0]])],"derivedFrom":subQ1}),-1.0]])]});}
            var Q67;
            {var subQ0=sQuery(id+"F0.wireOp",EDGE,"E23.right");var subQ1=sQuery(id+"F0.wireOp",EDGE,"E9");var subQ2=makeQuery(id+"F0.imprint","INTERSECT",VERTEX,{"derivedFrom":[subQ1,subQ0]});Q67=makeQuery(id+"F0.imprint","IMPRINT",FACE,{"disambiguationData":[TD([[makeQuery(id+"F0.imprint","IMPRINT",EDGE,{"disambiguationData":[TD([[subQ2,-1.0]])],"derivedFrom":subQ1}),1.0]])]});}
            var Q68;
            {var subQ0=sQuery(id+"F0.wireOp",EDGE,"E9");var subQ1=sQuery(id+"F0.wireOp",EDGE,"E0.right");var subQ2=makeQuery(id+"F0.imprint","INTERSECT",VERTEX,{"derivedFrom":[subQ1,subQ0]});Q68=makeQuery(id+"F0.imprint","IMPRINT",FACE,{"disambiguationData":[TD([[makeQuery(id+"F0.imprint","IMPRINT",EDGE,{"disambiguationData":[TD([[subQ2,1.0]])],"derivedFrom":subQ1}),-1.0]])]});}
            var Q69;
            {var subQ0=sQuery(id+"F0.wireOp",EDGE,"E23.right");var subQ1=sQuery(id+"F0.wireOp",EDGE,"E11");var subQ2=makeQuery(id+"F0.imprint","INTERSECT",VERTEX,{"derivedFrom":[subQ1,subQ0]});Q69=makeQuery(id+"F0.imprint","IMPRINT",FACE,{"disambiguationData":[TD([[makeQuery(id+"F0.imprint","IMPRINT",EDGE,{"disambiguationData":[TD([[subQ2,-1.0]])],"derivedFrom":subQ1}),1.0]])]});}
            var Q70;
            {var subQ0=sQuery(id+"F0.wireOp",EDGE,"E11");var subQ1=sQuery(id+"F0.wireOp",EDGE,"E0.right");var subQ2=makeQuery(id+"F0.imprint","INTERSECT",VERTEX,{"derivedFrom":[subQ1,subQ0]});Q70=makeQuery(id+"F0.imprint","IMPRINT",FACE,{"disambiguationData":[TD([[makeQuery(id+"F0.imprint","IMPRINT",EDGE,{"disambiguationData":[TD([[subQ2,1.0]])],"derivedFrom":subQ1}),-1.0]])]});}
            extrude(context, id + "F1", {"entities" : qUnion([Q0, Q1, Q2, Q3, Q4, Q5, Q6, Q7, Q8, Q9, Q10, Q11, Q12, Q13, Q14, Q15, Q16, Q17, Q18, Q19, Q20, Q21, Q22, Q23, Q24, Q25, Q26, Q27, Q28, Q29, Q30, Q31, Q32, Q33, Q34, Q35, Q36, Q37, Q38, Q39, Q40, Q41, Q42, Q43, Q44, Q45, Q46, Q47, Q48, Q49, Q50, Q51, Q52, Q53, Q54, Q55, Q56, Q57, Q58, Q59, Q60, Q61, Q62, Q63, Q64, Q65, Q66, Q67, Q68, Q69, Q70]), "depth" : 457.2 * mm, "offsetDistance" : 25.4 * mm});
        }
    });
